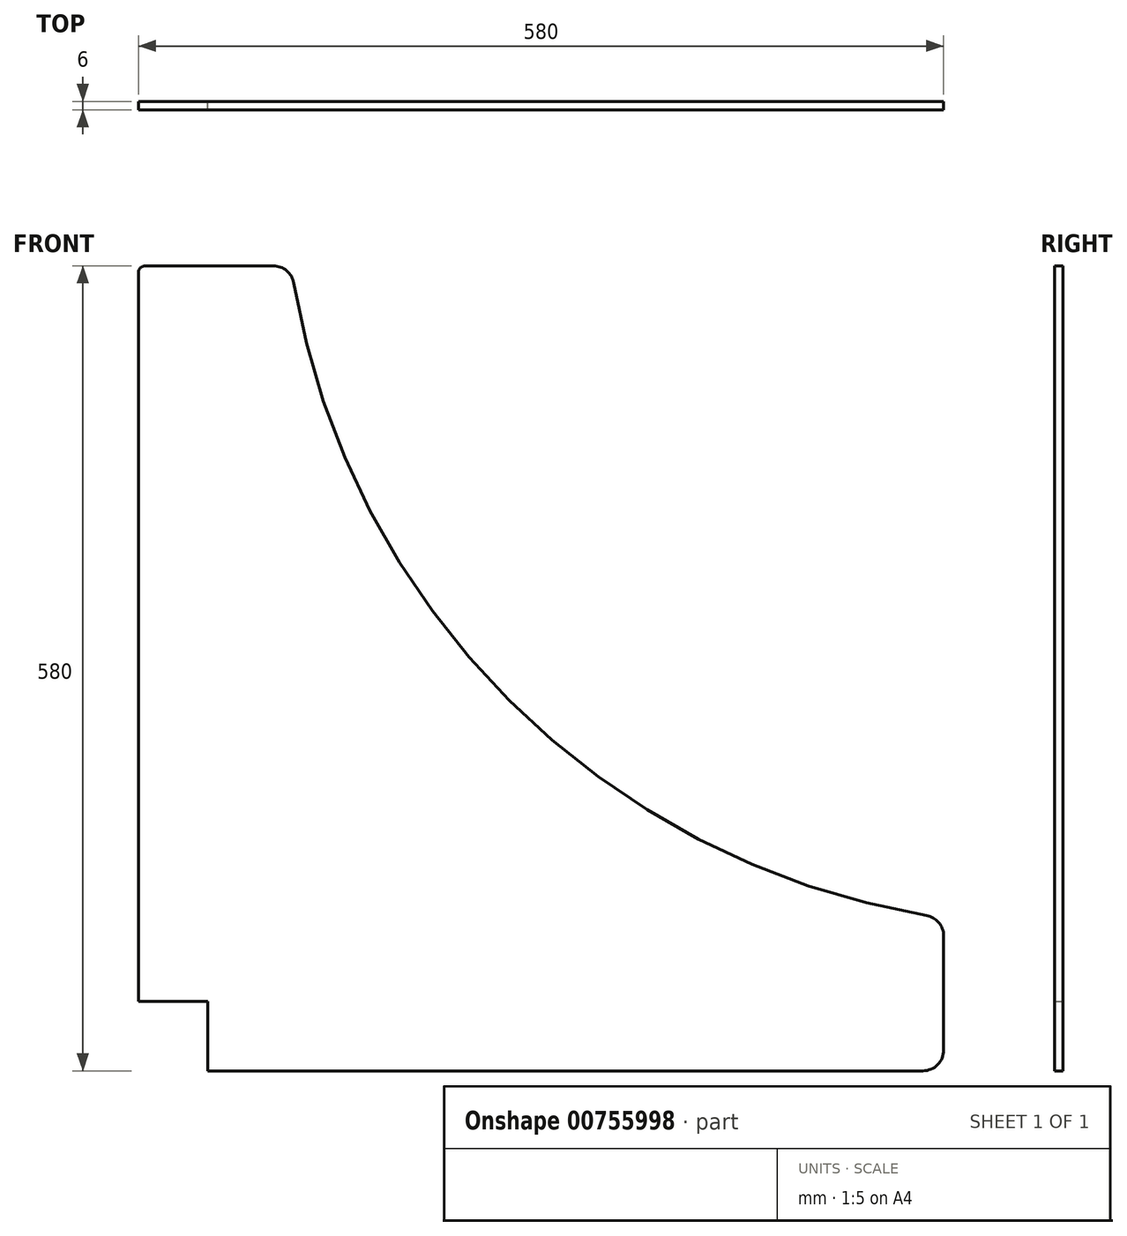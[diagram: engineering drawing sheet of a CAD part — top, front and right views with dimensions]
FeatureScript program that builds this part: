
annotation { "Feature Type Name" : "Feature", "Feature Type Description" : "" }
export const myFeature = defineFeature(function(context is Context, id is Id, definition is map)
    precondition{}
    {
        {
            var Q0;
            Q0=qCreatedBy(makeId("Front.planeOp"),FACE);
            var sketch = newSketch(context, id + "F0", { "sketchPlane" : qUnion([Q0])});
            skLineSegment(sketch, "E0.bottom", {"start": v(0, 0) * mm, "end": v(580, 0) * mm});
            skLineSegment(sketch, "E0.top", {"start": v(0, 580) * mm, "end": v(580, 580) * mm});
            skLineSegment(sketch, "E0.left", {"start": v(0, 0) * mm, "end": v(0, 580) * mm});
            skLineSegment(sketch, "E0.right", {"start": v(580, 0) * mm, "end": v(580, 580) * mm});
            skLineSegment(sketch, "E1", {"start": v(0, 50) * mm, "end": v(50, 50) * mm});
            skLineSegment(sketch, "E2", {"start": v(50, 50) * mm, "end": v(50, 0) * mm});
            skLineSegment(sketch, "E3", {"start": v(110, 580) * mm, "end": v(580, 110) * mm});
            skArc(sketch, "E4", {"start": v(110, 580) * mm, "mid": v(267, 267) * mm, "end": v(580, 110) * mm});
            skSolve(sketch);
        }
        {
            var Q0;
            {var subQ3=sQuery(id+"F0.wireOp",EDGE,"E1");Q0=makeQuery(id+"F0.imprint","IMPRINT",FACE,{"disambiguationData":[TD([[makeQuery(id+"F0.imprint","IMPRINT",EDGE,{"derivedFrom":subQ3}),1.0]])]});}
            extrude(context, id + "F1", {"entities" : qUnion([Q0]), "depth" : 5 * mm, "offsetDistance" : 25 * mm});
        }
        {
            var Q0;
            {var subQ3=sQuery(id+"F0.wireOp",EDGE,"E1");Q0=makeQuery(id+"F0.imprint","IMPRINT",FACE,{"disambiguationData":[TD([[makeQuery(id+"F0.imprint","IMPRINT",EDGE,{"derivedFrom":subQ3}),1.0]])]});}
            extrude(context, id + "F2", {"entities" : qUnion([Q0]), "operationType" : NewBodyOperationType.ADD, "depth" : 6 * mm, "offsetDistance" : 25 * mm});
        }
        {
            var Q0;
            {var subQ0=sQuery(id+"F0.wireOp",EDGE,"E0.right");var subQ1=sQuery(id+"F0.wireOp",EDGE,"E0.bottom");Q0=makeQuery(id+"F2.boolean.opBoolean","MERGE",EDGE,{"derivedFrom":[makeQuery(id+"F1.opExtrude","SWEPT_EDGE",EDGE,{"disambiguationData":[OSD([subQ1,subQ0])]}),makeQuery(id+"F2.opExtrude","SWEPT_EDGE",EDGE,{"disambiguationData":[OSD([subQ1,subQ0])]})]});}
            var Q1;
            {var subQ0=sQuery(id+"F0.wireOp",EDGE,"E4");var subQ1=sQuery(id+"F0.wireOp",EDGE,"E3");var subQ2=sQuery(id+"F0.wireOp",EDGE,"E0.right");Q1=makeQuery(id+"F2.boolean.opBoolean","MERGE",EDGE,{"derivedFrom":[makeQuery(id+"F1.opExtrude","SWEPT_EDGE",EDGE,{"disambiguationData":[OSD([subQ2,subQ1,subQ0])]}),makeQuery(id+"F2.opExtrude","SWEPT_EDGE",EDGE,{"disambiguationData":[OSD([subQ2,subQ1,subQ0])]})]});}
            fillet(context, id + "F3", {"entities" : qUnion([Q0, Q1]), "radius" : 15 * mm, "tangentPropagation" : true, "allowEdgeOverflow" : false});
        }
        {
            var Q0;
            {var subQ0=sQuery(id+"F0.wireOp",EDGE,"E4");var subQ1=sQuery(id+"F0.wireOp",EDGE,"E3");var subQ2=sQuery(id+"F0.wireOp",EDGE,"E0.top");Q0=makeQuery(id+"F2.boolean.opBoolean","MERGE",EDGE,{"derivedFrom":[makeQuery(id+"F1.opExtrude","SWEPT_EDGE",EDGE,{"disambiguationData":[OSD([subQ2,subQ1,subQ0])]}),makeQuery(id+"F2.opExtrude","SWEPT_EDGE",EDGE,{"disambiguationData":[OSD([subQ2,subQ1,subQ0])]})]});}
            fillet(context, id + "F4", {"entities" : qUnion([Q0]), "radius" : 15 * mm, "tangentPropagation" : true, "allowEdgeOverflow" : false});
        }
        {
            var Q0;
            {var subQ0=sQuery(id+"F0.wireOp",EDGE,"E0.left");var subQ1=sQuery(id+"F0.wireOp",EDGE,"E0.top");Q0=makeQuery(id+"F2.boolean.opBoolean","MERGE",EDGE,{"derivedFrom":[makeQuery(id+"F1.opExtrude","SWEPT_EDGE",EDGE,{"disambiguationData":[OSD([subQ1,subQ0])]}),makeQuery(id+"F2.opExtrude","SWEPT_EDGE",EDGE,{"disambiguationData":[OSD([subQ1,subQ0])]})]});}
            fillet(context, id + "F5", {"entities" : qUnion([Q0]), "radius" : 5 * mm, "tangentPropagation" : true, "allowEdgeOverflow" : false});
        }
    });
